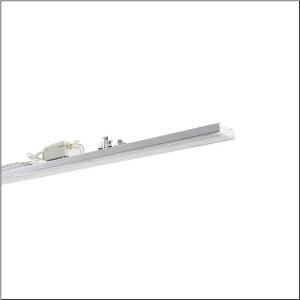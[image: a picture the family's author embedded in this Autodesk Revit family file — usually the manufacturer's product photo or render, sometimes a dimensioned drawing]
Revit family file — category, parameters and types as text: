
# Revit family: licross_r__21_recessed_mo_52te127n485g_14fa
name_source: partatom
category: Lighting Fixtures
units: mm (PartAtom-declared; Revit-internal decimal feet)

## family parameters
Cut with Voids When Loaded = No
Host = Face
Light Source = No
Part Type = Normal
Room Calculation Point = No
Round Connector Dimension = Use Diameter
Shared = No

## types (1)
- Licross® 21 Recessed MO (1 x LED, 8820 lm, 47.9 W, 4000K)
    Apparent Load = 48 VA
    CIE Flux Codes = 72 92 99 100 100
    Color Rendering = 80
    Color Temperature = 4000K
    Default Elevation = 1800 mm
    Description = Licross® 21 Recessed MO, luminaire insert, of sheet steel, galvanised, coil coated, white, length: 1.500mm, width: 66mm, height: 67mm, LED rated luminous flux: 8.820lm, light colour: 840, control gear: ON/OFF, with plug, 3-pole, with phase selection, mains connection: 220..240V, AC, 50/60Hz, rated input power: 48W, halogen-free wiring, primary optical cover: cover, of PMMA, light emission: direct distribution, primary light characteristic: symmetric, protection rating (complete): IP54, insulation class (complete): insulation class I (protective earthing), certification: CE, ENEC, VDE, UKCA, protection symbol: D if used in an environment with non-conductive dust loads with corresponding accessories, impact resistance: IK06, permissible ambient temperature for indoor applications: -35..+40°C, corresponds to IFS (International Featured Standards) requirements for safety and quality in the food industry, reducing of maximum allowable ambient temperature of 5°C with ceiling mounting, LABS conformity tested according to VDMA 24364:2018-05, packaging unit: 1 piece
    Height = 58 mm
    Lamp = 1 x LED
    Lamp Light Flux = 8820 lm
    Lamp Power = 47.9 W
    Lamp count = 1
    Length = 1500 mm
    Luminous efficacy = 184 lm/W
    Manufacturer = Siteco
    ModVariant = No
    Model = 52TE127N485G
    Mounting Place = Ceiling
    Mounting Type = Pendant
    Number of Poles = 1
    OnlyDefault = Yes
    Power Factor = 1
    Product Name = Licross® 21 Recessed MO
    Product group = luminaire insert
    ProductGroupID = 901
    Protection Class = Protection class I
    Protection Degree = IP 54
    RLX_Detail_Level = 1
    RLX_Emergency_Light_Flux = 0 lm
    RLX_Emergency_Type = 0
    RLX_Emergency_Type_DB = No
    RlxData = <blob elided: 20905 chars, md5=b1e4cfeb>
    Socket = socket
    Standby Power = 0 W
    System Light Flux = 8820 lm
    System Power = 48 W
    Type Comments = Product without accessories
    Type Image = l_1296930.jpg
    URL = http://relux.com
    VarID = ---
    Voltage = 0 V
    Weight = 0.00 kg
    Width = 66 mm

## geometry (parser evidence)
native form markers: Blend x4, Sweep x10
no freeform markers — native parametric forms only
